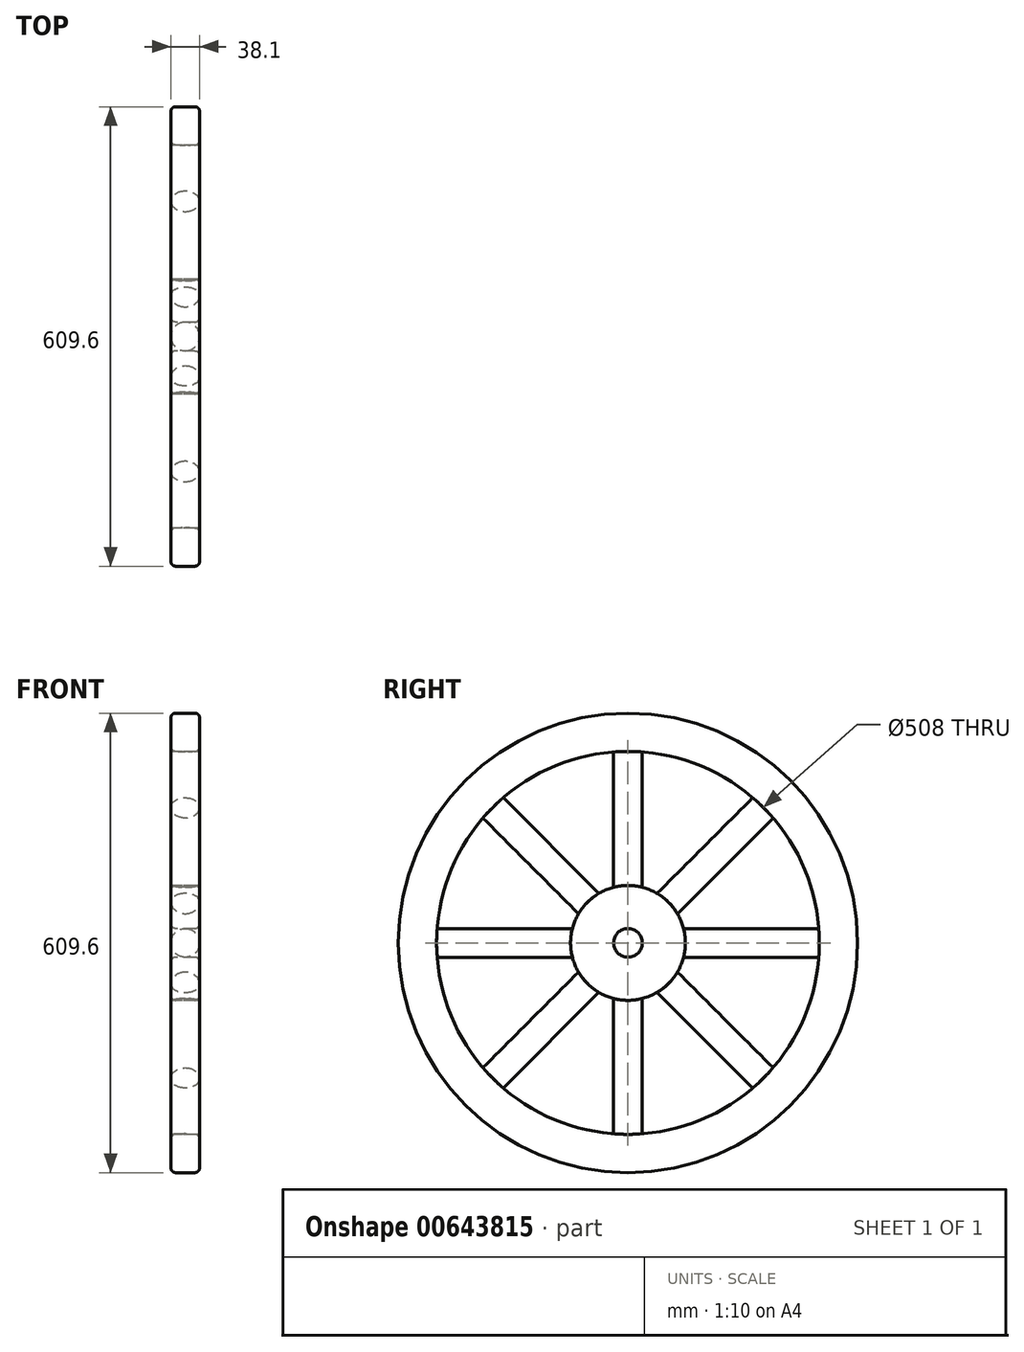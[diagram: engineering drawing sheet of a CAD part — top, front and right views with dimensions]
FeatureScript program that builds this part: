
annotation { "Feature Type Name" : "Feature", "Feature Type Description" : "" }
export const myFeature = defineFeature(function(context is Context, id is Id, definition is map)
    precondition{}
    {
        {
            var Q0;
            Q0=qCreatedBy(makeId("Right.planeOp"),FACE);
            var sketch = newSketch(context, id + "F0", { "sketchPlane" : qUnion([Q0])});
            skCircle(sketch, "E0", {"center": v(0, 0) * mm, "radius": 304.8 * mm});
            skCircle(sketch, "E1", {"center": v(0, 0) * mm, "radius": 254 * mm});
            skSolve(sketch);
        }
        {
            var Q0;
            Q0 = qSketchRegion(id + "F0", true);
            extrude(context, id + "F1", {"entities" : qUnion([Q0]), "endBound" : BoundingType.SYMMETRIC, "depth" : 38.1 * mm, "offsetDistance" : 25.4 * mm});
        }
        {
            var Q0;
            Q0=qCreatedBy(makeId("Right.planeOp"),FACE);
            var sketch = newSketch(context, id + "F2", { "sketchPlane" : qUnion([Q0])});
            skCircle(sketch, "E2", {"center": v(0, 0) * mm, "radius": 19.05 * mm});
            skCircle(sketch, "E3", {"center": v(0, 0) * mm, "radius": 76.2 * mm});
            skSolve(sketch);
        }
        {
            var Q0;
            Q0 = qSketchRegion(id + "F2", true);
            extrude(context, id + "F3", {"entities" : qUnion([Q0]), "endBound" : BoundingType.SYMMETRIC, "depth" : 38.1 * mm, "offsetDistance" : 25.4 * mm});
        }
        {
            var Q0;
            Q0=makeQuery(id+"F1.opExtrude","CAP_EDGE",EDGE,{"disambiguationData":[OSD([sQuery(id+"F0.wireOp",EDGE,"E0")])],"isStart":false});
            var Q1;
            Q1=makeQuery(id+"F1.opExtrude","CAP_EDGE",EDGE,{"disambiguationData":[OSD([sQuery(id+"F0.wireOp",EDGE,"E0")])],"isStart":true});
            var Q2;
            Q2=makeQuery(id+"F1.opExtrude","CAP_EDGE",EDGE,{"disambiguationData":[OSD([sQuery(id+"F0.wireOp",EDGE,"E1")])],"isStart":false});
            var Q3;
            Q3=makeQuery(id+"F1.opExtrude","CAP_EDGE",EDGE,{"disambiguationData":[OSD([sQuery(id+"F0.wireOp",EDGE,"E1")])],"isStart":true});
            var Q4;
            Q4=makeQuery(id+"F3.opExtrude","CAP_EDGE",EDGE,{"disambiguationData":[OSD([sQuery(id+"F2.wireOp",EDGE,"E3")])],"isStart":true});
            var Q5;
            Q5=makeQuery(id+"F3.opExtrude","CAP_EDGE",EDGE,{"disambiguationData":[OSD([sQuery(id+"F2.wireOp",EDGE,"E3")])],"isStart":false});
            var Q6;
            Q6=makeQuery(id+"F3.opExtrude","CAP_EDGE",EDGE,{"disambiguationData":[OSD([sQuery(id+"F2.wireOp",EDGE,"E2")])],"isStart":false});
            var Q7;
            Q7=makeQuery(id+"F3.opExtrude","CAP_EDGE",EDGE,{"disambiguationData":[OSD([sQuery(id+"F2.wireOp",EDGE,"E2")])],"isStart":true});
            fillet(context, id + "F4", {"entities" : qUnion([Q0, Q1, Q2, Q3, Q4, Q5, Q6, Q7]), "radius" : 6.35 * mm, "tangentPropagation" : true, "allowEdgeOverflow" : false});
        }
        {
            var Q0;
            Q0=qCreatedBy(makeId("Right.planeOp"),FACE);
            var sketch = newSketch(context, id + "F5", { "sketchPlane" : qUnion([Q0])});
            skLineSegment(sketch, "E4", {"start": v(0, 0) * mm, "end": v(19.05, 0) * mm});
            skLineSegment(sketch, "E5", {"start": v(0, 0) * mm, "end": v(-19.05, 0) * mm});
            skArc(sketch, "E6", {"start": v(19.05, 253.28) * mm, "mid": v(0, 254) * mm, "end": v(-19.05, 253.28) * mm});
            skLineSegment(sketch, "E7", {"start": v(-19.05, 73.78) * mm, "end": v(-19.05, 253.28) * mm});
            skLineSegment(sketch, "E8", {"start": v(19.05, 73.78) * mm, "end": v(19.05, 253.28) * mm});
            skArc(sketch, "E9", {"start": v(19.05, 73.78) * mm, "mid": v(0, 76.2) * mm, "end": v(-19.05, 73.78) * mm});
            skArc(sketch, "E10.1.0", {"start": v(-38.7, 65.64) * mm, "mid": v(-53.88, 53.88) * mm, "end": v(-65.64, 38.7) * mm});
            skLineSegment(sketch, "E10.1.1", {"start": v(-65.64, 38.7) * mm, "end": v(-192.57, 165.63) * mm});
            skArc(sketch, "E10.1.2", {"start": v(-165.63, 192.57) * mm, "mid": v(-179.6, 179.6) * mm, "end": v(-192.57, 165.63) * mm});
            skLineSegment(sketch, "E10.1.3", {"start": v(-38.7, 65.64) * mm, "end": v(-165.63, 192.57) * mm});
            skArc(sketch, "E10.2.0", {"start": v(-73.78, 19.05) * mm, "mid": v(-76.2, 0) * mm, "end": v(-73.78, -19.05) * mm});
            skLineSegment(sketch, "E10.2.1", {"start": v(-73.78, -19.05) * mm, "end": v(-253.28, -19.05) * mm});
            skArc(sketch, "E10.2.2", {"start": v(-253.28, 19.05) * mm, "mid": v(-254, 0) * mm, "end": v(-253.28, -19.05) * mm});
            skLineSegment(sketch, "E10.2.3", {"start": v(-73.78, 19.05) * mm, "end": v(-253.28, 19.05) * mm});
            skArc(sketch, "E10.3.0", {"start": v(-65.64, -38.7) * mm, "mid": v(-53.88, -53.88) * mm, "end": v(-38.7, -65.64) * mm});
            skLineSegment(sketch, "E10.3.1", {"start": v(-38.7, -65.64) * mm, "end": v(-165.63, -192.57) * mm});
            skArc(sketch, "E10.3.2", {"start": v(-192.57, -165.63) * mm, "mid": v(-179.6, -179.6) * mm, "end": v(-165.63, -192.57) * mm});
            skLineSegment(sketch, "E10.3.3", {"start": v(-65.64, -38.7) * mm, "end": v(-192.57, -165.63) * mm});
            skArc(sketch, "E10.4.0", {"start": v(-19.05, -73.78) * mm, "mid": v(0, -76.2) * mm, "end": v(19.05, -73.78) * mm});
            skLineSegment(sketch, "E10.4.1", {"start": v(19.05, -73.78) * mm, "end": v(19.05, -253.28) * mm});
            skArc(sketch, "E10.4.2", {"start": v(-19.05, -253.28) * mm, "mid": v(0, -254) * mm, "end": v(19.05, -253.28) * mm});
            skLineSegment(sketch, "E10.4.3", {"start": v(-19.05, -73.78) * mm, "end": v(-19.05, -253.28) * mm});
            skArc(sketch, "E10.5.0", {"start": v(38.7, -65.64) * mm, "mid": v(53.88, -53.88) * mm, "end": v(65.64, -38.7) * mm});
            skLineSegment(sketch, "E10.5.1", {"start": v(65.64, -38.7) * mm, "end": v(192.57, -165.63) * mm});
            skArc(sketch, "E10.5.2", {"start": v(165.63, -192.57) * mm, "mid": v(179.6, -179.6) * mm, "end": v(192.57, -165.63) * mm});
            skLineSegment(sketch, "E10.5.3", {"start": v(38.7, -65.64) * mm, "end": v(165.63, -192.57) * mm});
            skArc(sketch, "E10.6.0", {"start": v(73.78, -19.05) * mm, "mid": v(76.2, 0) * mm, "end": v(73.78, 19.05) * mm});
            skLineSegment(sketch, "E10.6.1", {"start": v(73.78, 19.05) * mm, "end": v(253.28, 19.05) * mm});
            skArc(sketch, "E10.6.2", {"start": v(253.28, -19.05) * mm, "mid": v(254, 0) * mm, "end": v(253.28, 19.05) * mm});
            skLineSegment(sketch, "E10.6.3", {"start": v(73.78, -19.05) * mm, "end": v(253.28, -19.05) * mm});
            skArc(sketch, "E10.7.0", {"start": v(65.64, 38.7) * mm, "mid": v(53.88, 53.88) * mm, "end": v(38.7, 65.64) * mm});
            skLineSegment(sketch, "E10.7.1", {"start": v(38.7, 65.64) * mm, "end": v(165.63, 192.57) * mm});
            skArc(sketch, "E10.7.2", {"start": v(192.57, 165.63) * mm, "mid": v(179.6, 179.6) * mm, "end": v(165.63, 192.57) * mm});
            skLineSegment(sketch, "E10.7.3", {"start": v(65.64, 38.7) * mm, "end": v(192.57, 165.63) * mm});
            skSolve(sketch);
        }
        {
            var Q0;
            Q0 = qSketchRegion(id + "F5", true);
            extrude(context, id + "F6", {"entities" : qUnion([Q0]), "endBound" : BoundingType.SYMMETRIC, "depth" : 38.1 * mm, "offsetDistance" : 25.4 * mm});
        }
        {
            var Q0;
            Q0=makeQuery(id+"F6.opExtrude","CAP_EDGE",EDGE,{"disambiguationData":[OSD([sQuery(id+"F5.wireOp",EDGE,"E8")])],"isStart":false});
            var Q1;
            Q1=makeQuery(id+"F6.opExtrude","CAP_EDGE",EDGE,{"disambiguationData":[OSD([sQuery(id+"F5.wireOp",EDGE,"E7")])],"isStart":false});
            var Q2;
            Q2=makeQuery(id+"F6.opExtrude","CAP_EDGE",EDGE,{"disambiguationData":[OSD([sQuery(id+"F5.wireOp",EDGE,"E7")])],"isStart":true});
            var Q3;
            Q3=makeQuery(id+"F6.opExtrude","CAP_EDGE",EDGE,{"disambiguationData":[OSD([sQuery(id+"F5.wireOp",EDGE,"E8")])],"isStart":true});
            var Q4;
            Q4=makeQuery(id+"F6.opExtrude","CAP_EDGE",EDGE,{"disambiguationData":[OSD([sQuery(id+"F5.wireOp",EDGE,"E10.1.3")])],"isStart":true});
            var Q5;
            Q5=makeQuery(id+"F6.opExtrude","CAP_EDGE",EDGE,{"disambiguationData":[OSD([sQuery(id+"F5.wireOp",EDGE,"E10.1.3")])],"isStart":false});
            var Q6;
            Q6=makeQuery(id+"F6.opExtrude","CAP_EDGE",EDGE,{"disambiguationData":[OSD([sQuery(id+"F5.wireOp",EDGE,"E10.1.1")])],"isStart":true});
            var Q7;
            Q7=makeQuery(id+"F6.opExtrude","CAP_EDGE",EDGE,{"disambiguationData":[OSD([sQuery(id+"F5.wireOp",EDGE,"E10.1.1")])],"isStart":false});
            var Q8;
            Q8=makeQuery(id+"F6.opExtrude","CAP_EDGE",EDGE,{"disambiguationData":[OSD([sQuery(id+"F5.wireOp",EDGE,"E10.2.3")])],"isStart":false});
            var Q9;
            Q9=makeQuery(id+"F6.opExtrude","CAP_EDGE",EDGE,{"disambiguationData":[OSD([sQuery(id+"F5.wireOp",EDGE,"E10.2.3")])],"isStart":true});
            var Q10;
            Q10=makeQuery(id+"F6.opExtrude","CAP_EDGE",EDGE,{"disambiguationData":[OSD([sQuery(id+"F5.wireOp",EDGE,"E10.2.1")])],"isStart":true});
            var Q11;
            Q11=makeQuery(id+"F6.opExtrude","CAP_EDGE",EDGE,{"disambiguationData":[OSD([sQuery(id+"F5.wireOp",EDGE,"E10.2.1")])],"isStart":false});
            var Q12;
            Q12=makeQuery(id+"F6.opExtrude","CAP_EDGE",EDGE,{"disambiguationData":[OSD([sQuery(id+"F5.wireOp",EDGE,"E10.3.3")])],"isStart":false});
            var Q13;
            Q13=makeQuery(id+"F6.opExtrude","CAP_EDGE",EDGE,{"disambiguationData":[OSD([sQuery(id+"F5.wireOp",EDGE,"E10.3.1")])],"isStart":false});
            var Q14;
            Q14=makeQuery(id+"F6.opExtrude","CAP_EDGE",EDGE,{"disambiguationData":[OSD([sQuery(id+"F5.wireOp",EDGE,"E10.3.3")])],"isStart":true});
            var Q15;
            Q15=makeQuery(id+"F6.opExtrude","CAP_EDGE",EDGE,{"disambiguationData":[OSD([sQuery(id+"F5.wireOp",EDGE,"E10.3.1")])],"isStart":true});
            var Q16;
            Q16=makeQuery(id+"F6.opExtrude","CAP_EDGE",EDGE,{"disambiguationData":[OSD([sQuery(id+"F5.wireOp",EDGE,"E10.4.3")])],"isStart":true});
            var Q17;
            Q17=makeQuery(id+"F6.opExtrude","CAP_EDGE",EDGE,{"disambiguationData":[OSD([sQuery(id+"F5.wireOp",EDGE,"E10.4.3")])],"isStart":false});
            var Q18;
            Q18=makeQuery(id+"F6.opExtrude","CAP_EDGE",EDGE,{"disambiguationData":[OSD([sQuery(id+"F5.wireOp",EDGE,"E10.4.1")])],"isStart":false});
            var Q19;
            Q19=makeQuery(id+"F6.opExtrude","CAP_EDGE",EDGE,{"disambiguationData":[OSD([sQuery(id+"F5.wireOp",EDGE,"E10.4.1")])],"isStart":true});
            var Q20;
            Q20=makeQuery(id+"F6.opExtrude","CAP_EDGE",EDGE,{"disambiguationData":[OSD([sQuery(id+"F5.wireOp",EDGE,"E10.5.3")])],"isStart":true});
            var Q21;
            Q21=makeQuery(id+"F6.opExtrude","CAP_EDGE",EDGE,{"disambiguationData":[OSD([sQuery(id+"F5.wireOp",EDGE,"E10.5.1")])],"isStart":true});
            var Q22;
            Q22=makeQuery(id+"F6.opExtrude","CAP_EDGE",EDGE,{"disambiguationData":[OSD([sQuery(id+"F5.wireOp",EDGE,"E10.5.3")])],"isStart":false});
            var Q23;
            Q23=makeQuery(id+"F6.opExtrude","CAP_EDGE",EDGE,{"disambiguationData":[OSD([sQuery(id+"F5.wireOp",EDGE,"E10.5.1")])],"isStart":false});
            var Q24;
            Q24=makeQuery(id+"F6.opExtrude","CAP_EDGE",EDGE,{"disambiguationData":[OSD([sQuery(id+"F5.wireOp",EDGE,"E10.6.1")])],"isStart":false});
            var Q25;
            Q25=makeQuery(id+"F6.opExtrude","CAP_EDGE",EDGE,{"disambiguationData":[OSD([sQuery(id+"F5.wireOp",EDGE,"E10.6.3")])],"isStart":false});
            var Q26;
            Q26=makeQuery(id+"F6.opExtrude","CAP_EDGE",EDGE,{"disambiguationData":[OSD([sQuery(id+"F5.wireOp",EDGE,"E10.6.1")])],"isStart":true});
            var Q27;
            Q27=makeQuery(id+"F6.opExtrude","CAP_EDGE",EDGE,{"disambiguationData":[OSD([sQuery(id+"F5.wireOp",EDGE,"E10.6.3")])],"isStart":true});
            var Q28;
            Q28=makeQuery(id+"F6.opExtrude","CAP_EDGE",EDGE,{"disambiguationData":[OSD([sQuery(id+"F5.wireOp",EDGE,"E10.7.1")])],"isStart":true});
            var Q29;
            Q29=makeQuery(id+"F6.opExtrude","CAP_EDGE",EDGE,{"disambiguationData":[OSD([sQuery(id+"F5.wireOp",EDGE,"E10.7.3")])],"isStart":true});
            var Q30;
            Q30=makeQuery(id+"F6.opExtrude","CAP_EDGE",EDGE,{"disambiguationData":[OSD([sQuery(id+"F5.wireOp",EDGE,"E10.7.3")])],"isStart":false});
            var Q31;
            Q31=makeQuery(id+"F6.opExtrude","CAP_EDGE",EDGE,{"disambiguationData":[OSD([sQuery(id+"F5.wireOp",EDGE,"E10.7.1")])],"isStart":false});
            fillet(context, id + "F7", {"entities" : qUnion([Q0, Q1, Q2, Q3, Q4, Q5, Q6, Q7, Q8, Q9, Q10, Q11, Q12, Q13, Q14, Q15, Q16, Q17, Q18, Q19, Q20, Q21, Q22, Q23, Q24, Q25, Q26, Q27, Q28, Q29, Q30, Q31]), "radius" : 19.05 * mm, "tangentPropagation" : true, "allowEdgeOverflow" : false});
        }
    });
